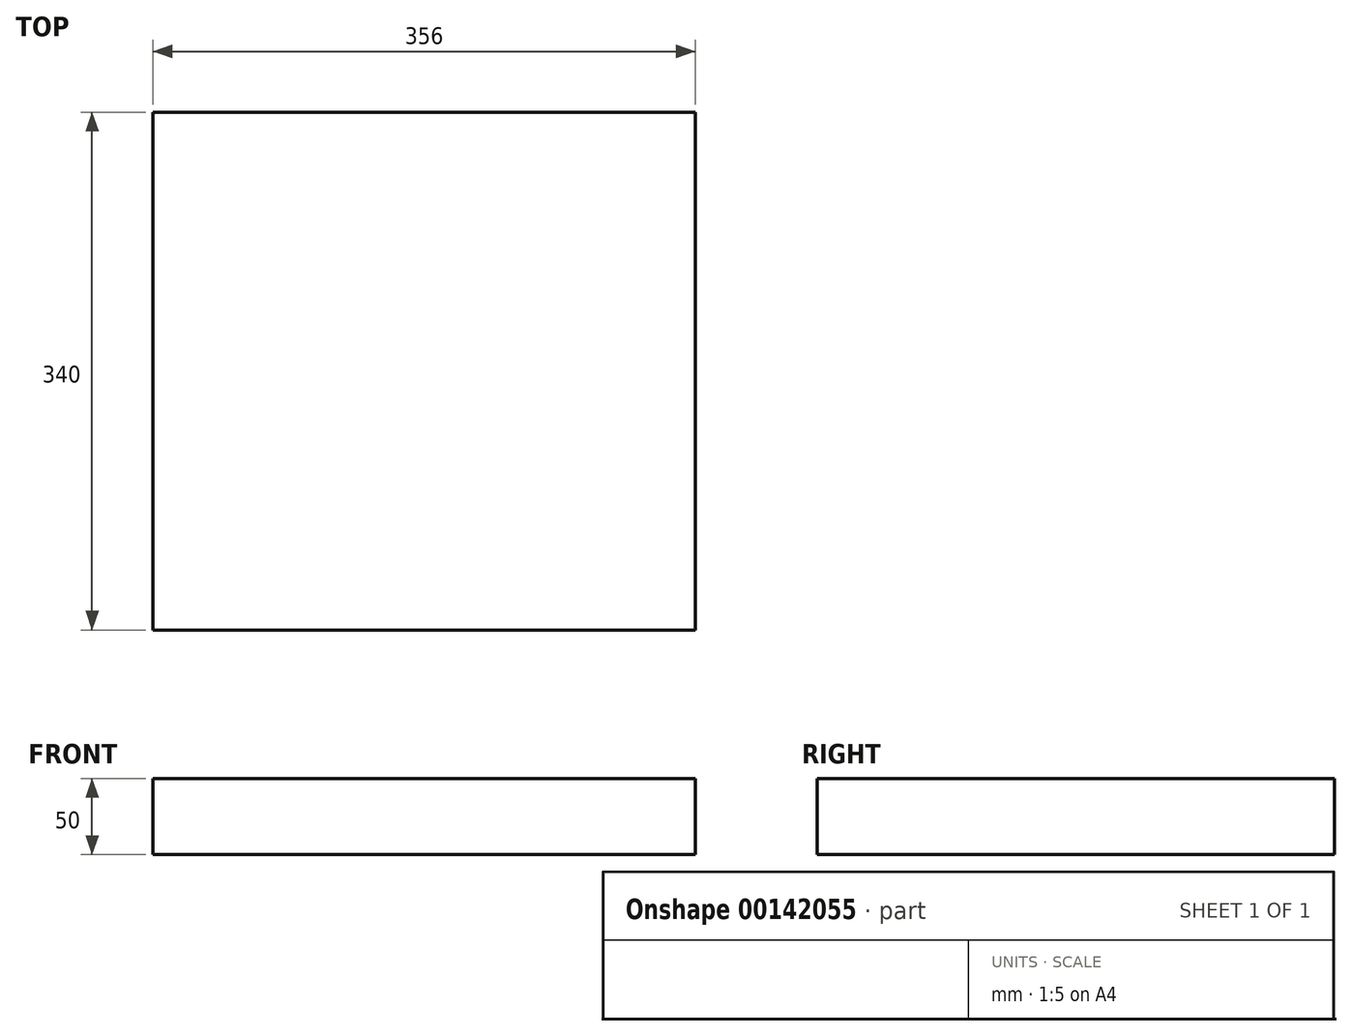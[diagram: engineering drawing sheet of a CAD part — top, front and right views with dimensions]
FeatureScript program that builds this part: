
annotation { "Feature Type Name" : "Feature", "Feature Type Description" : "" }
export const myFeature = defineFeature(function(context is Context, id is Id, definition is map)
    precondition{}
    {
        {
            var Q0;
            Q0=qCreatedBy(makeId("Top.planeOp"),FACE);
            var sketch = newSketch(context, id + "F0", { "sketchPlane" : qUnion([Q0])});
            skLineSegment(sketch, "E0.bottom", {"start": v(-171.44, 182.5) * mm, "end": v(184.56, 182.5) * mm});
            skLineSegment(sketch, "E0.top", {"start": v(-171.44, -157.5) * mm, "end": v(184.56, -157.5) * mm});
            skLineSegment(sketch, "E0.left", {"start": v(-171.44, 182.5) * mm, "end": v(-171.44, -157.5) * mm});
            skLineSegment(sketch, "E0.right", {"start": v(184.56, 182.5) * mm, "end": v(184.56, -157.5) * mm});
            skSolve(sketch);
        }
        {
            var Q0;
            Q0 = qSketchRegion(id + "F0", true);
            extrude(context, id + "F1", {"entities" : qUnion([Q0]), "depth" : 50 * mm});
        }
    });
